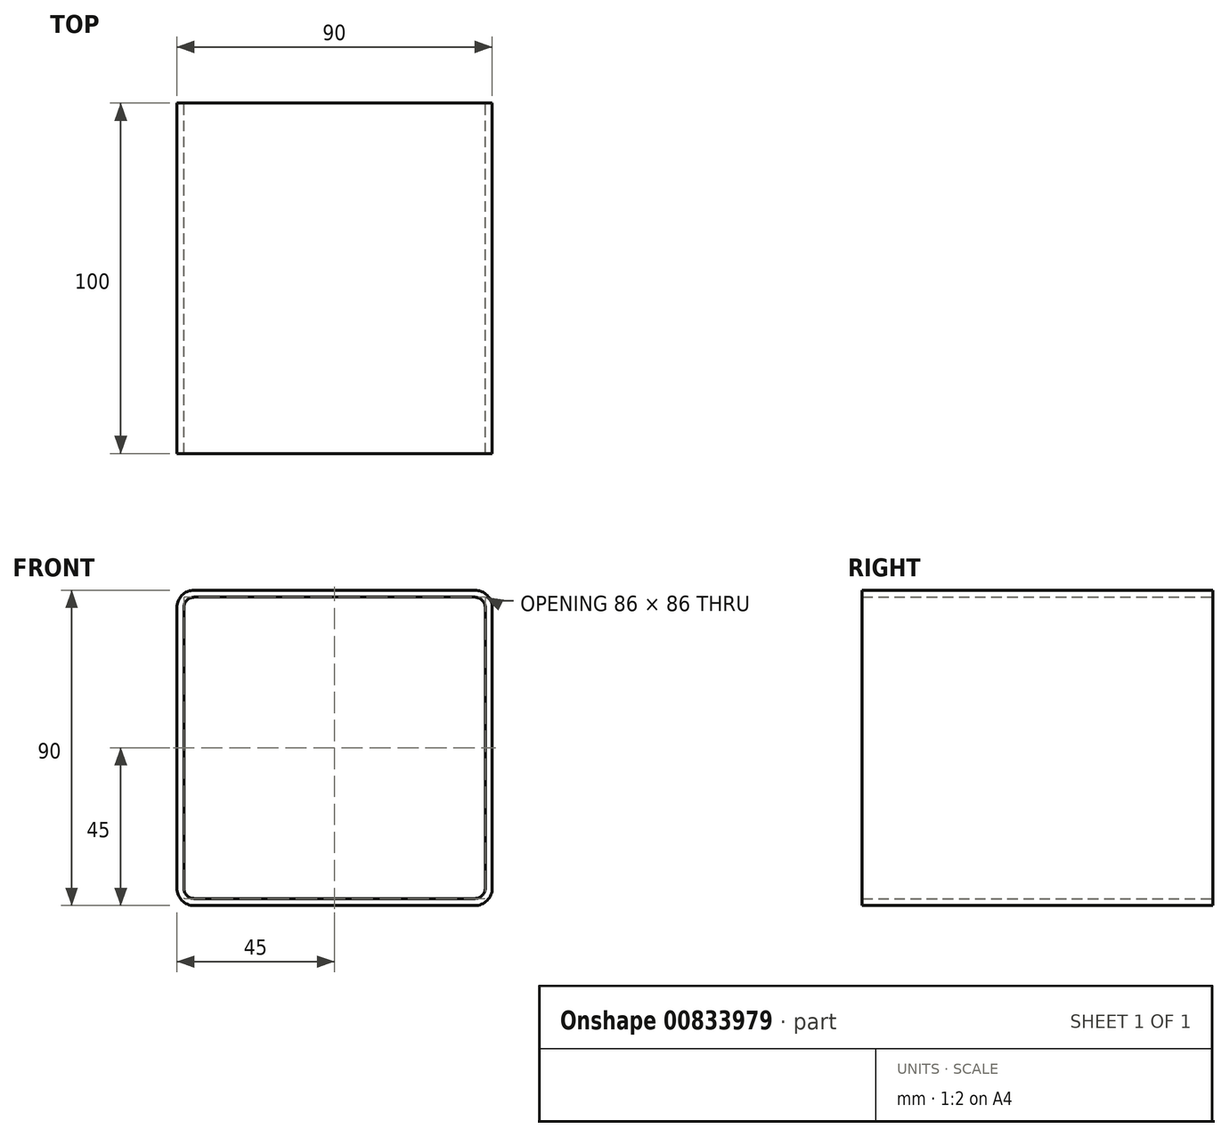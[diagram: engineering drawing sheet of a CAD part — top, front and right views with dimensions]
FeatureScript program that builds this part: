
annotation { "Feature Type Name" : "Feature", "Feature Type Description" : "" }
export const myFeature = defineFeature(function(context is Context, id is Id, definition is map)
    precondition{}
    {
        {
            var Q0;
            Q0=qCreatedBy(makeId("Front.planeOp"),FACE);
            var sketch = newSketch(context, id + "F0", { "sketchPlane" : qUnion([Q0])});
            skLineSegment(sketch, "E0.bottom", {"start": v(45, 45) * mm, "end": v(-45, 45) * mm});
            skLineSegment(sketch, "E0.top", {"start": v(45, -45) * mm, "end": v(-45, -45) * mm});
            skLineSegment(sketch, "E0.left", {"start": v(45, 45) * mm, "end": v(45, -45) * mm});
            skLineSegment(sketch, "E0.right", {"start": v(-45, 45) * mm, "end": v(-45, -45) * mm});
            skPoint(sketch, "E0.middle", {"position": v(0, 0) * mm});
            skLineSegment(sketch, "E1.bottom", {"start": v(43, 43) * mm, "end": v(-43, 43) * mm});
            skLineSegment(sketch, "E1.top", {"start": v(43, -43) * mm, "end": v(-43, -43) * mm});
            skLineSegment(sketch, "E1.left", {"start": v(43, 43) * mm, "end": v(43, -43) * mm});
            skLineSegment(sketch, "E1.right", {"start": v(-43, 43) * mm, "end": v(-43, -43) * mm});
            skSolve(sketch);
        }
        {
            var Q0;
            Q0=makeQuery(id+"F0.imprint","IMPRINT",FACE,{"disambiguationData":[TD([[makeQuery(id+"F0.imprint","IMPRINT",EDGE,{"derivedFrom":sQuery(id+"F0.wireOp",EDGE,"E0.bottom")}),1.0]])]});
            extrude(context, id + "F1", {"entities" : qUnion([Q0]), "depth" : 100 * mm, "offsetDistance" : 25 * mm});
        }
        {
            var Q0;
            Q0=makeQuery(id+"F1.opExtrude","SWEPT_EDGE",EDGE,{"disambiguationData":[OSD([sQuery(id+"F0.wireOp",EDGE,"E0.bottom"),sQuery(id+"F0.wireOp",EDGE,"E0.left")])]});
            var Q1;
            Q1=makeQuery(id+"F1.opExtrude","SWEPT_EDGE",EDGE,{"disambiguationData":[OSD([sQuery(id+"F0.wireOp",EDGE,"E0.bottom"),sQuery(id+"F0.wireOp",EDGE,"E0.right")])]});
            var Q2;
            Q2=makeQuery(id+"F1.opExtrude","SWEPT_EDGE",EDGE,{"disambiguationData":[OSD([sQuery(id+"F0.wireOp",EDGE,"E0.top"),sQuery(id+"F0.wireOp",EDGE,"E0.left")])]});
            var Q3;
            Q3=makeQuery(id+"F1.opExtrude","SWEPT_EDGE",EDGE,{"disambiguationData":[OSD([sQuery(id+"F0.wireOp",EDGE,"E0.top"),sQuery(id+"F0.wireOp",EDGE,"E0.right")])]});
            fillet(context, id + "F2", {"entities" : qUnion([Q0, Q1, Q2, Q3]), "radius" : 5 * mm, "tangentPropagation" : true, "allowEdgeOverflow" : false});
        }
        {
            var Q0;
            Q0=makeQuery(id+"F1.opExtrude","SWEPT_EDGE",EDGE,{"disambiguationData":[OSD([sQuery(id+"F0.wireOp",EDGE,"E1.bottom"),sQuery(id+"F0.wireOp",EDGE,"E1.right")])]});
            var Q1;
            Q1=makeQuery(id+"F1.opExtrude","SWEPT_EDGE",EDGE,{"disambiguationData":[OSD([sQuery(id+"F0.wireOp",EDGE,"E1.bottom"),sQuery(id+"F0.wireOp",EDGE,"E1.left")])]});
            var Q2;
            Q2=makeQuery(id+"F1.opExtrude","SWEPT_EDGE",EDGE,{"disambiguationData":[OSD([sQuery(id+"F0.wireOp",EDGE,"E1.top"),sQuery(id+"F0.wireOp",EDGE,"E1.right")])]});
            var Q3;
            Q3=makeQuery(id+"F1.opExtrude","SWEPT_EDGE",EDGE,{"disambiguationData":[OSD([sQuery(id+"F0.wireOp",EDGE,"E1.top"),sQuery(id+"F0.wireOp",EDGE,"E1.left")])]});
            fillet(context, id + "F3", {"entities" : qUnion([Q0, Q1, Q2, Q3]), "radius" : 3 * mm, "tangentPropagation" : true, "allowEdgeOverflow" : false});
        }
    });
